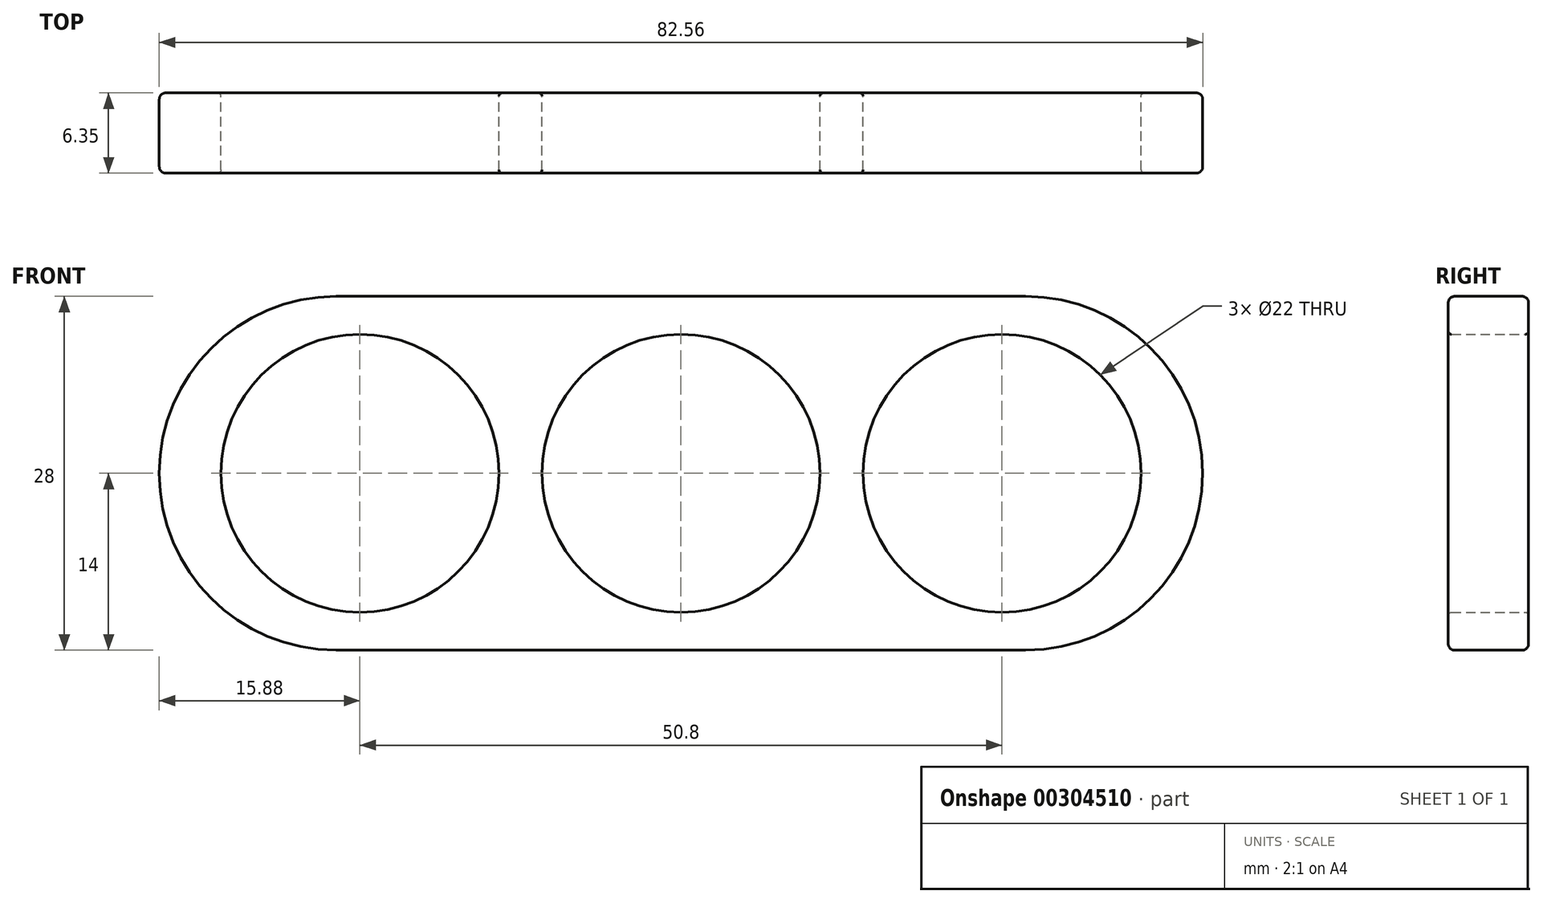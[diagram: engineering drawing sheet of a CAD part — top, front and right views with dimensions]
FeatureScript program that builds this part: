
annotation { "Feature Type Name" : "Feature", "Feature Type Description" : "" }
export const myFeature = defineFeature(function(context is Context, id is Id, definition is map)
    precondition{}
    {
        {
            var Q0;
            Q0=qCreatedBy(makeId("Front.planeOp"),FACE);
            var sketch = newSketch(context, id + "F0", { "sketchPlane" : qUnion([Q0])});
            skLineSegment(sketch, "E0.bottom", {"start": v(27.28, -14) * mm, "end": v(-27.28, -14) * mm});
            skLineSegment(sketch, "E0.top", {"start": v(27.28, 14) * mm, "end": v(-27.28, 14) * mm});
            skLineSegment(sketch, "E0.left", {"start": v(41.28, 0) * mm, "end": v(41.28, 0) * mm});
            skLineSegment(sketch, "E0.right", {"start": v(-41.28, 0) * mm, "end": v(-41.28, 0) * mm});
            skPoint(sketch, "E0.middle", {"position": v(0, 0) * mm});
            skCircle(sketch, "E1", {"center": v(0, 0) * mm, "radius": 11 * mm});
            skPoint(sketch, "E2.middle", {"position": v(-25.4, 0) * mm});
            skCircle(sketch, "E3", {"center": v(-25.4, 0) * mm, "radius": 11 * mm});
            skPoint(sketch, "E4.middle", {"position": v(25.4, 0) * mm});
            skCircle(sketch, "E5", {"center": v(25.4, 0) * mm, "radius": 11 * mm});
            skPoint(sketch, "E6.visualSharp", {"position": v(-41.28, 14) * mm});
            skArc(sketch, "E6.filletArc", {"start": v(-27.28, 14) * mm, "mid": v(-37.17, 9.9) * mm, "end": v(-41.28, 0) * mm});
            skPoint(sketch, "E7.visualSharp", {"position": v(-41.28, -14) * mm});
            skArc(sketch, "E7.filletArc", {"start": v(-41.28, 0) * mm, "mid": v(-37.17, -9.9) * mm, "end": v(-27.28, -14) * mm});
            skPoint(sketch, "E8.visualSharp", {"position": v(41.28, -14) * mm});
            skArc(sketch, "E8.filletArc", {"start": v(27.28, -14) * mm, "mid": v(37.17, -9.9) * mm, "end": v(41.28, 0) * mm});
            skPoint(sketch, "E9.visualSharp", {"position": v(41.28, 14) * mm});
            skArc(sketch, "E9.filletArc", {"start": v(41.28, 0) * mm, "mid": v(37.17, 9.9) * mm, "end": v(27.28, 14) * mm});
            skSolve(sketch);
        }
        {
            var Q0;
            Q0=makeQuery(id+"F0.imprint","IMPRINT",FACE,{"disambiguationData":[TD([[makeQuery(id+"F0.imprint","IMPRINT",EDGE,{"derivedFrom":sQuery(id+"F0.wireOp",EDGE,"E0.bottom")}),-1.0]])]});
            extrude(context, id + "F1", {"entities" : qUnion([Q0]), "depth" : 6.35 * mm});
        }
        {
            var Q0;
            Q0=makeQuery(id+"F1.opExtrude","CAP_EDGE",EDGE,{"disambiguationData":[OSD([sQuery(id+"F0.wireOp",EDGE,"E0.top")])],"isStart":false});
            var Q1;
            Q1=makeQuery(id+"F1.opExtrude","CAP_EDGE",EDGE,{"disambiguationData":[OSD([sQuery(id+"F0.wireOp",EDGE,"E0.top")])],"isStart":true});
            fillet(context, id + "F2", {"entities" : qUnion([Q0, Q1]), "radius" : 0.5 * mm, "tangentPropagation" : true, "allowEdgeOverflow" : false});
        }
        {
            var Q0;
            Q0=makeQuery(id+"F1.opExtrude","CAP_EDGE",EDGE,{"disambiguationData":[OSD([sQuery(id+"F0.wireOp",EDGE,"E5")])],"isStart":false});
            var Q1;
            Q1=makeQuery(id+"F1.opExtrude","CAP_EDGE",EDGE,{"disambiguationData":[OSD([sQuery(id+"F0.wireOp",EDGE,"E1")])],"isStart":false});
            var Q2;
            Q2=makeQuery(id+"F1.opExtrude","CAP_EDGE",EDGE,{"disambiguationData":[OSD([sQuery(id+"F0.wireOp",EDGE,"E3")])],"isStart":false});
            var Q3;
            Q3=makeQuery(id+"F1.opExtrude","CAP_EDGE",EDGE,{"disambiguationData":[OSD([sQuery(id+"F0.wireOp",EDGE,"E3")])],"isStart":true});
            var Q4;
            Q4=makeQuery(id+"F1.opExtrude","CAP_EDGE",EDGE,{"disambiguationData":[OSD([sQuery(id+"F0.wireOp",EDGE,"E1")])],"isStart":true});
            var Q5;
            Q5=makeQuery(id+"F1.opExtrude","CAP_EDGE",EDGE,{"disambiguationData":[OSD([sQuery(id+"F0.wireOp",EDGE,"E5")])],"isStart":true});
            fillet(context, id + "F3", {"entities" : qUnion([Q0, Q1, Q2, Q3, Q4, Q5]), "radius" : 0.25 * mm, "tangentPropagation" : true, "allowEdgeOverflow" : false});
        }
    });
